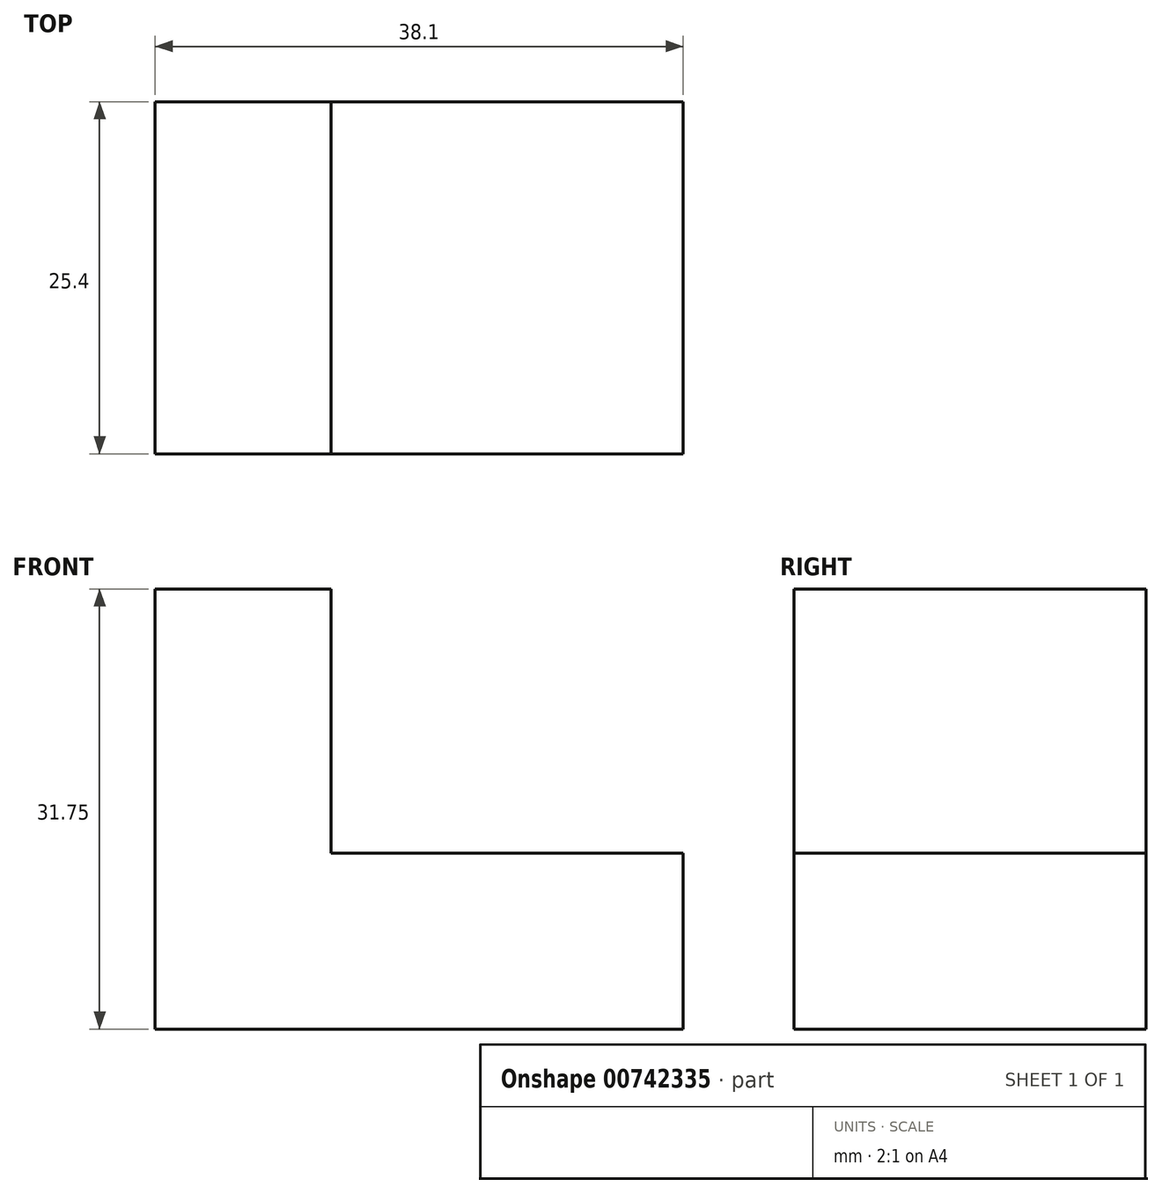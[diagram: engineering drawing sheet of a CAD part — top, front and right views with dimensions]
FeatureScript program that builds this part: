
annotation { "Feature Type Name" : "Feature", "Feature Type Description" : "" }
export const myFeature = defineFeature(function(context is Context, id is Id, definition is map)
    precondition{}
    {
        {
            var Q0;
            Q0=qCreatedBy(makeId("Front.planeOp"),FACE);
            var sketch = newSketch(context, id + "F0", { "sketchPlane" : qUnion([Q0])});
            skLineSegment(sketch, "E0", {"start": v(0, 0) * mm, "end": v(-38.1, 0) * mm});
            skLineSegment(sketch, "E1", {"start": v(-38.1, 0) * mm, "end": v(-38.1, 31.75) * mm});
            skLineSegment(sketch, "E2", {"start": v(-38.1, 31.75) * mm, "end": v(-25.4, 31.75) * mm});
            skLineSegment(sketch, "E3", {"start": v(-25.4, 31.75) * mm, "end": v(-25.4, 12.7) * mm});
            skLineSegment(sketch, "E4", {"start": v(-25.4, 12.7) * mm, "end": v(0, 12.7) * mm});
            skLineSegment(sketch, "E5", {"start": v(0, 12.7) * mm, "end": v(0, 0) * mm});
            skSolve(sketch);
        }
        {
            var Q0;
            Q0 = qSketchRegion(id + "F0", true);
            extrude(context, id + "F1", {"entities" : qUnion([Q0]), "depth" : 25.4 * mm, "offsetDistance" : 25.4 * mm});
        }
    });
